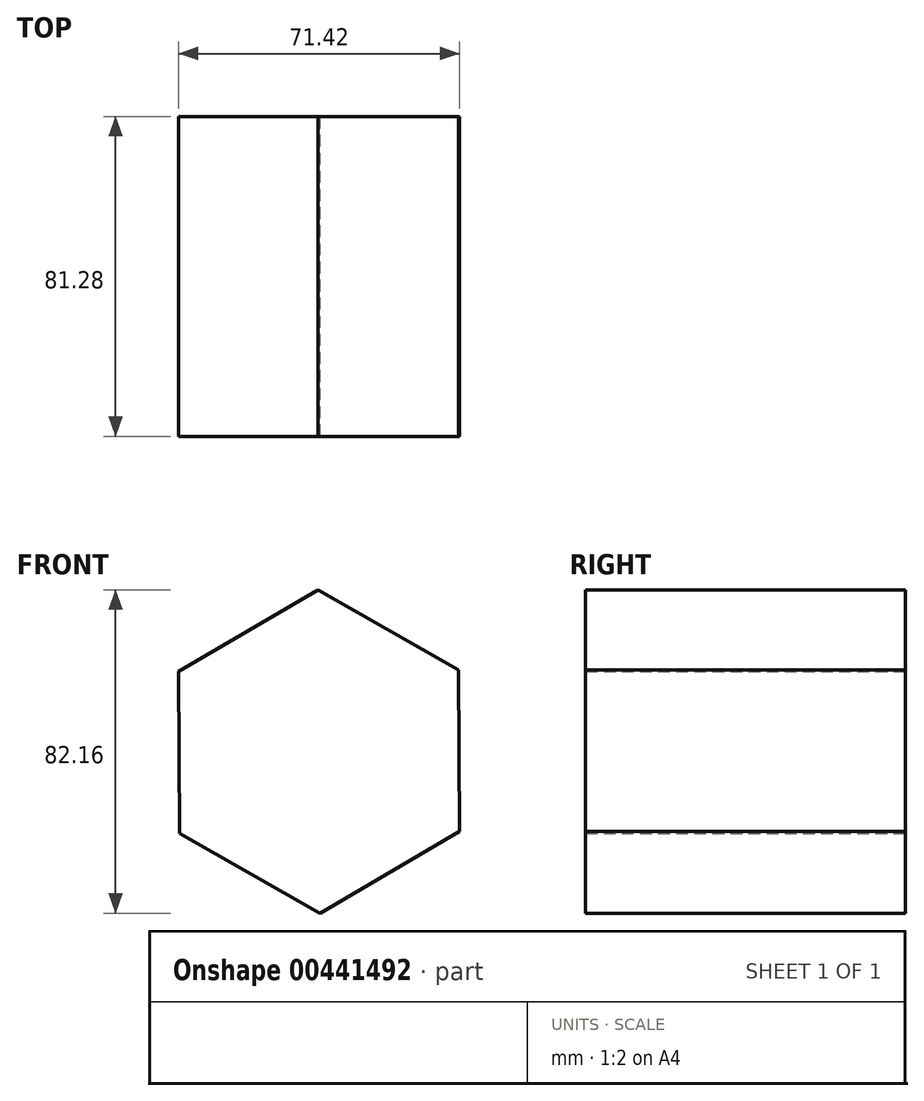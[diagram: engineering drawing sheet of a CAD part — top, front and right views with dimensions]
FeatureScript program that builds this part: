
annotation { "Feature Type Name" : "Feature", "Feature Type Description" : "" }
export const myFeature = defineFeature(function(context is Context, id is Id, definition is map)
    precondition{}
    {
        {
            var Q0;
            Q0=qCreatedBy(makeId("Front.planeOp"),FACE);
            var sketch = newSketch(context, id + "F0", { "sketchPlane" : qUnion([Q0])});
            skCircle(sketch, "E0.cCircle", {"center": v(0, 0) * mm, "radius": 35.58 * mm, "construction": true});
            skLineSegment(sketch, "E0.0", {"start": v(-0.26, 41.08) * mm, "end": v(35.45, 20.77) * mm});
            skLineSegment(sketch, "E0.1", {"start": v(35.45, 20.77) * mm, "end": v(35.71, -20.31) * mm});
            skLineSegment(sketch, "E0.2", {"start": v(35.71, -20.31) * mm, "end": v(0.26, -41.08) * mm});
            skLineSegment(sketch, "E0.3", {"start": v(0.26, -41.08) * mm, "end": v(-35.45, -20.77) * mm});
            skLineSegment(sketch, "E0.4", {"start": v(-35.45, -20.77) * mm, "end": v(-35.71, 20.31) * mm});
            skLineSegment(sketch, "E0.5", {"start": v(-35.71, 20.31) * mm, "end": v(-0.26, 41.08) * mm});
            skPoint(sketch, "E0.0.midPoint", {"position": v(17.6, 30.93) * mm});
            skSolve(sketch);
        }
        {
            var Q0;
            Q0=makeQuery(id+"F0.imprint","IMPRINT",FACE,{"disambiguationData":[TD([[makeQuery(id+"F0.imprint","IMPRINT",EDGE,{"derivedFrom":sQuery(id+"F0.wireOp",EDGE,"E0.0")}),-1.0]])]});
            extrude(context, id + "F1", {"entities" : qUnion([Q0]), "depth" : 81.28 * mm});
        }
    });
